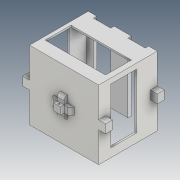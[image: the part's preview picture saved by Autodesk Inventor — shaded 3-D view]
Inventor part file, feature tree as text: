
AUTODESK INVENTOR PART (.ipt)
format: ipt  version: 2021 (Build 250183000, 183)  size: 357,888 bytes
history: native  units: mm
features: extrude x19, sketch x19, other x1, fillet x1
ambient origin geometry x8: Origin, YZ Plane, XZ Plane, XY Plane, X Axis, Y Axis, Z Axis, Center Point
bodies: Body1 (feature_tree), Body2 (feature_tree), Body3 (feature_tree), Body4 (feature_tree)
feature tree (40):
  other  "Sólido1"
  extrude  "Extrusão1"  Depth=40.0mm
  extrude  "Extrusão2"  Depth=10.0mm TaperAngle=0.0deg
  extrude  "Extrusão3"  Depth=20.0mm TaperAngle=0.0deg
  extrude  "Extrusão4"  Depth=5.0mm TaperAngle=0.0deg
  extrude  "Extrusão5"  Depth=5.0mm TaperAngle=0.0deg
  extrude  "Extrusão6"  Depth=5.0mm
  extrude  "Extrusão7"  Depth=4.0mm TaperAngle=0.0deg
  extrude  "Extrusão8"  Depth=10.0mm
  extrude  "Extrusão9"  Depth=10.0mm TaperAngle=0.0deg
  extrude  "Extrusão11"  Depth=4.0mm
  extrude  "Extrusão12"  Depth=5.0mm
  extrude  "Extrusão15"  Depth=5.0mm
  extrude  "Extrusão16"  Depth=4.0mm TaperAngle=0.0deg
  extrude  "Extrusão17"  Depth=2.0mm
  extrude  "Extrusão18"  TaperAngle=0.0deg  [1 undecoded]
  extrude  "Extrusão19"  [1 undecoded]
  extrude  "Extrusão20"  [1 undecoded]
  extrude  "Extrusão21"  [1 undecoded]
  fillet  "Arredondamento1"  [1 undecoded]
  extrude  "Extrusão22"  [1 undecoded]
  sketch  "Esboço1"  dims[d0=40.0mm d1=40.0mm]
  sketch  "Esboço2"  dims[d2=2.0mm d3=0.0mm d4=10.0mm d5=0.0mm]
  sketch  "Esboço3"  dims[d6=20.0mm d7=0.0mm d8=20.0mm d9=0.0mm]
  sketch  "Esboço4"  dims[d10=20.0mm d11=0.0mm d12=5.0mm d13=0.0mm]
  sketch  "Esboço6"  dims[d14=5.0mm d15=0.0mm d16=5.0mm d17=0.0mm]
  sketch  "Esboço7"  dims[d18=2.0mm d19=0.0mm d30=5.0mm]
  sketch  "Esboço8"  dims[d31=4.0mm d32=0.0mm d34=4.0mm d35=0.0mm]
  sketch  "Esboço9"  dims[d44=10.0mm d45=10.0mm]
  sketch  "Esboço10"  dims[d46=40.0mm d47=10.0mm d48=0.0mm]
  sketch  "Esboço14"  dims[d49=4.0mm d50=0.0mm d51=4.0mm]
  sketch  "Esboço15"  dims[d52=4.0mm d53=0.0mm d54=5.0mm]
  sketch  "Esboço20"  dims[d55=4.0mm d56=0.0mm d57=5.0mm]
  sketch  "Esboço21"  dims[d58=4.0mm d59=0.0mm d60=4.0mm d61=0.0mm]
  sketch  "Esboço22"  dims[d62=2.0mm d63=0.0mm d64=2.0mm]
  sketch  "Esboço23"  dims[d65=1.0mm d66=0.0mm d67=0.0mm]
  sketch  "Esboço24"  dims[d33=0.5mm]
  sketch  "Esboço26"
  sketch  "Esboço27"
  sketch  "Esboço30"
note: 6 required parameter values undecoded (feature->parameter linkage not recoverable at this tier; creation-order binding heuristic only, values carry confidence <= 0.55)
